# Revit family: WVA-12
name_source: partatom
category: Mechanical Equipment
revit_build: Autodesk Revit MEP 2014 (Build: 20140709_2115(x64)
units: mm (PartAtom-declared; Revit-internal decimal feet)

## types (1)
- WVA-12
    A = 32"
    ApproximateShipmentWeight = 1500lbs
    ArrayRadius = 14"
    B = 76"
    BottomExtrusionHeight = 7/8"
    BottomRevolveHeight = 8 1/4"
    C = 42 1/2"
    CouplingHeight = 11 3/4"
    CylindarDia = 22 3/8"
    CylinderHalfLength = 16"
    CylinderHeight = 59 3/8"
    D = 38"
    DrainExtrusionPosition = 2 3/4"
    Height1 = 2 1/2"
    Height2 = 3/8"
    HookDiameter = 3/4"
    HookDistance = 6 1/4"
    HookTopDistance = 1"
    HookWidth = 1 7/8"
    LeftHookDistance = 3/8"
    Manufacturer = Wessels Company
    MaximumFlow = 2100 GPM
    MaximumOperatingPressure = 125 PSIG
    MaximumOperatingTemperature = 240°F
    Model = WVA-12
    NumberOfArray = 9
    PartNumber = 72080120
    PipeConnectorDiameter = 12"
    PipeDiameter = 12 3/4"
    RevolveRadius = 11 1/4"
    RingDistance = 14 7/8"
    SideDrainExtrusion = 2 1/8"
    SideFlangeStep1 = 14 3/8"
    SideFlangeStep2 = 19 1/8"
    SideFlangeThickness = 1 1/8"
    SideFlangeThickness1 = 1"
    Step1Diameter = 1 3/4"
    Step2Diameter = 3 1/2"
    Step3Diameter = 5 7/8"
    Step4Diameter = 8 1/8"
    Step5Diameter = 7"
    TopExtrusionDiameter = 3 1/2"
    TotalHeight = 10 3/8"
    URL = http://westank.com

## geometry (parser evidence)
native form markers: Extrusion x4, Revolve x1, Sweep x5
no freeform markers — native parametric forms only
